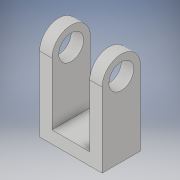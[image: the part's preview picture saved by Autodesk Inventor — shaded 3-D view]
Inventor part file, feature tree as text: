
AUTODESK INVENTOR PART (.ipt)
format: ipt  version: 2017 (Build 210142000, 142)  size: 120,832 bytes
history: native  units: in
note: dims shown in document units (in); Inventor stores cm internally (conversion verified against a paired STEP export)
features: extrude x2, sketch x2
ambient origin geometry x8: Origin, YZ Plane, XZ Plane, XY Plane, X Axis, Y Axis, Z Axis, Center Point
bodies: Solid1 (feature_tree)
feature tree (4):
  extrude  "Extrusion1"  Depth=0.77in
  extrude  "Extrusion2"  Depth=0.77in
  sketch  "Sketch1"  dims[d0=0.5in d1=0.77in]
  sketch  "Sketch2"  dims[d2=1.5in d3=0.77in d4=1.26in d5=0.0in d6=0.76in d7=1.635in d8=0.25in d9=0.25in d10=1.26in d11=0.0in]
